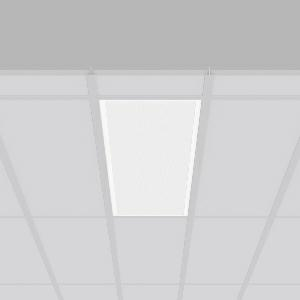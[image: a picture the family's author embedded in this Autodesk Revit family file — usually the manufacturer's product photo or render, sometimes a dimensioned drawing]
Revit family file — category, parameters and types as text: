
# Revit family: sidelite_eco_672369_002_07_70d9
name_source: partatom
category: Lighting Fixtures
units: mm (PartAtom-declared; Revit-internal decimal feet)

## family parameters
Cut with Voids When Loaded = No
Host = Face
Light Source = No
Part Type = Normal
Room Calculation Point = No
Round Connector Dimension = Use Diameter
Shared = No

## types (1)
- SIDELITE ECO (1 x LED Modul 830, 3200 lm, 3000)
    Apparent Load = 29 VA
    CIE Flux Codes = 59 87 97 100 100
    Color Rendering = 80
    Color Temperature = 3000
    Default Elevation = 1800 mm
    Description = Series: SIDELITE ECO
Highly economical recessed luminaire with progressive LED technology. For escape route illumination. Frame made of aluminium, powder-coated. Diffuser plastic microprismatic. Lightguide and diffuser made of non-yellowing plastic (PMMA). Lateral light emission (RZB SIDELITE technology) for homogeneous light distribution. External driver. Self-contained system with automatic self-test and feedback via DALI bus, only to RZB DALI monitoring system. External driver with simple plug-in locking system. Extended connection cable (1.90 m). 
Colour: white
Length: 1195 mm
Width: 295 mm
Cut-out length: 1170 mm
Cut-out width: 270 mm
Recess height: 160 mm
Luminaire: recess height: 40 mm
Weight: 4.4 kg
Operating mode: maintained power mode
Duration time: 8 h
Lamp: LED
Socket: without socket
Colour temperature: 3000K
Colour rendering index (CRI): 80
System power: 29 W
Rated luminous flux: 3200 lm
Luminous flux, emergency: 220 lm
System power, emergency: -
Control gear: Regulated power supply
Protection class: I
Type of protection: IP 40
    Height = 0 mm  [stored 0 ft]
    Lamp = 1 x LED Modul 830
    Lamp Light Flux = 3200 lm
    Lamp count = 1
    Length = 1195 mm
    Lifetime = 50000 h
    Luminous efficacy = 110 lm/W
    Manufacturer = RZB
    ModVariant = No
    Model = 672369.002.07
    Mounting Place = Ceiling
    Mounting Type = Recessed
    Number of Poles = 1
    OnlyDefault = Yes
    Power Factor = 1
    Product Name = SIDELITE ECO
    Product group = Recessed modular luminaires
    ProductGroupID = 406
    Protection Class = Protection class I
    Protection Degree = IP 40
    RLX_Detail_Level = 1
    RLX_Emergency_Light_Flux = 220 lm
    RLX_Emergency_Type = 3
    RLX_Emergency_Type_DB = Yes
    RlxData = <blob elided: 34757 chars, md5=49132cee>
    Socket = socket
    Standby Power = 0 W
    System Light Flux = 3200 lm
    System Power = 29 W
    Type Comments = Product without accessories
    Type Image = 312366.002.jpg
    URL = http://relux.com
    VarID = ---
    Voltage = 230 V
    Voltage Range = 220-240 V
    Weight = 0.00 kg
    Width = 295 mm

note: [stored X ft] marks values corroborated as IEEE doubles in the binary element streams (Revit-internal decimal feet)

## geometry (parser evidence)
native form markers: Blend x4, Sweep x12
no freeform markers — native parametric forms only
